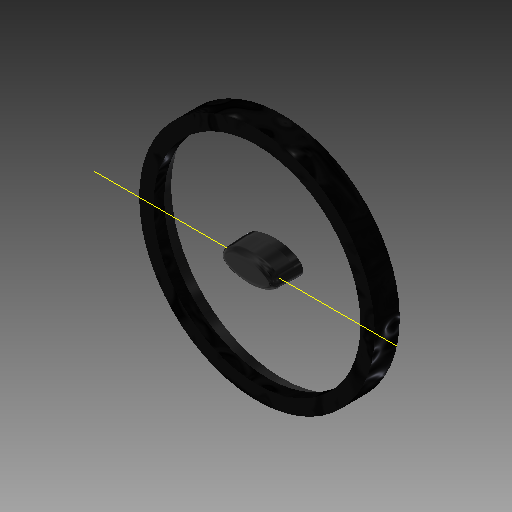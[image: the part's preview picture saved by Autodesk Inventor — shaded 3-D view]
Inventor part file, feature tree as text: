
AUTODESK INVENTOR PART (.ipt)
format: ipt  version: 2017 (Build 210142000, 142)  size: 712,192 bytes
history: native  units: in
note: dims shown in document units (in); Inventor stores cm internally (conversion verified against a paired STEP export)
features: sketch x24, extrude x18, plane x9, projected_geometry x5, loft x4, other x4, mirror x1, emboss x1, fillet x1, reference x1
ambient origin geometry x8: Origin, YZ Plane, XZ Plane, XY Plane, X Axis, Y Axis, Z Axis, Center Point
bodies: Solid1 (feature_tree)
feature tree (68):
  sketch  "Sketch1"  dims[d0=0.7559in d1=0.7559in]
  plane  "Work Plane1"
  loft  "Loft1"
  extrude  "Extrusion1"  Depth=0.2in
  plane  "Work Plane4"
  loft  "Loft2"
  plane  "Work Plane5"
  loft  "Loft3"
  loft  "Loft4"
  extrude  "Extrusion2"  TaperAngle=0.0deg  [1 undecoded]
  plane  "Work Plane6"
  extrude  "Extrusion3"  Depth=1.0in
  extrude  "Extrusion4"  Depth=1.0651in
  extrude  "Extrusion5"  Depth=0.962in
  plane  "Work Plane7"
  extrude  "Extrusion6"  Depth=0.075in
  plane  "Work Plane8"
  other  "Work Axis1"
  plane  "Work Plane9"
  extrude  "Extrusion7"  Depth=0.06in
  mirror  "Mirror3"
  extrude  "Extrusion8"  Depth=0.05in
  plane  "Work Plane10"
  extrude  "Extrusion9"  Depth=0.0625in
  plane  "Work Plane11"
  extrude  "Extrusion10"  Depth=0.075in
  extrude  "Extrusion11"  TaperAngle=0.0deg  [1 undecoded]
  extrude  "Extrusion12"  Depth=0.2in
  extrude  "Extrusion13"  TaperAngle=0.0deg  [1 undecoded]
  emboss  "Emboss1"
  extrude  "Extrusion16"  Depth=0.01in
  extrude  "Extrusion17"  Depth=0.0344in
  extrude  "Extrusion18"  TaperAngle=60.0deg  [1 undecoded]
  fillet  "Fillet1"  [1 undecoded]
  extrude  "Extrusion20"  Depth=0.05in
  other  "Work Axis3"
  extrude  "Extrusion21"  Depth=0.05in
  sketch  "Sketch2"  dims[d2=0.9963in d3=0.2in]
  sketch  "Sketch3"  dims[d4=0.5in d6=0.08in]
  sketch  "Sketch4"  dims[d7=0.55in d8=150.0deg]
  other  "Edges1"
  sketch  "Sketch5"  dims[d9=150.0deg d14=0.33in]
  projected_geometry  "Projected Loop1"
  other  "Edges2"
  sketch  "Sketch6"  dims[d15=0.66in d18=0.0in d19=90.0deg]
  sketch  "Sketch7"  dims[d20=0.0in d21=90.0deg d22=1.0in]
  sketch  "Sketch8"  dims[d26=1.0651in d28=1.0651in]
  sketch  "Sketch9"  dims[d29=0.0in d30=0.962in]
  sketch  "Sketch10"  dims[d31=0.962in d32=0.075in]
  sketch  "Sketch11"  dims[d33=0.15in d34=0.06in]
  sketch  "Sketch12"  dims[d35=0.1in d36=0.05in]
  sketch  "Sketch13"  dims[d37=0.45in d38=0.0in d39=0.0625in]
  projected_geometry  "Projected Loop2"
  projected_geometry  "Projected Loop3"
  sketch  "Sketch14"  dims[d40=0.01in d41=0.075in]
  projected_geometry  "Projected Loop4"
  sketch  "Sketch15"  dims[d42=0.01in d43=0.0in d44=90.0deg]
  sketch  "Sketch16"  dims[d45=0.0in d46=90.0deg d47=0.2in]
  sketch  "Sketch17"  dims[d48=0.07in d49=0.0in d50=90.0deg]
  sketch  "Sketch18"  dims[d51=0.0in d52=90.0deg d53=0.01in]
  sketch  "Sketch19"  dims[d54=0.01in d55=0.0344in]
  sketch  "Sketch23"  dims[d56=150.0deg d57=60.0deg d58=150.0deg]
  projected_geometry  "Projected Loop6"
  sketch  "Sketch24"  dims[d59=0.7in d60=0.05in]
  sketch  "Sketch25"  dims[d61=0.05in d62=0.05in d63=0.05in]
  sketch  "Sketch27"  dims[d64=0.05in]
  sketch  "Sketch28"  dims[d65=0.01in d66=0.0in d67=90.0deg d68=0.0in d69=90.0deg d70=0.1in d71=0.4in d72=0.15in d73=0.05in d74=0.0in d75=0.02in d77=0.15in d78=0.02in d79=0.1in d80=0.1in d81=0.1in d82=0.02in d83=0.15in d84=0.05in d85=0.0in d86=0.045in d87=0.0in d88=0.025in d89=0.0in d90=0.02in d91=0.02in d92=0.005in d93=0.0in d94=90.0deg d95=0.4466in d96=1.0in d97=0.0in d98=1.0in d99=0.0in d100=0.6528in d101=0.0in d102=0.0in d103=1.0in d104=0.0in d106=90.0deg d107=1.0in d108=0.0in d109=1.65in d110=0.1in d111=0.1in d112=0.0in d113=0.1in d114=0.075in d115=0.0in d116=0.05in d117=0.0in d123=0.84in d124=0.8in d125=0.0in d126=0.0in d127=1.0in d128=0.0in d130=0.15in d131=-0.0206in d135=0.2in d136=0.05in d137=0.1in d140=0.05in d141=0.1in d142=0.0in d143=0.05in d144=0.0in]
  reference  "Reference1"
note: 5 required parameter values undecoded (feature->parameter linkage not recoverable at this tier; creation-order binding heuristic only, values carry confidence <= 0.55)
